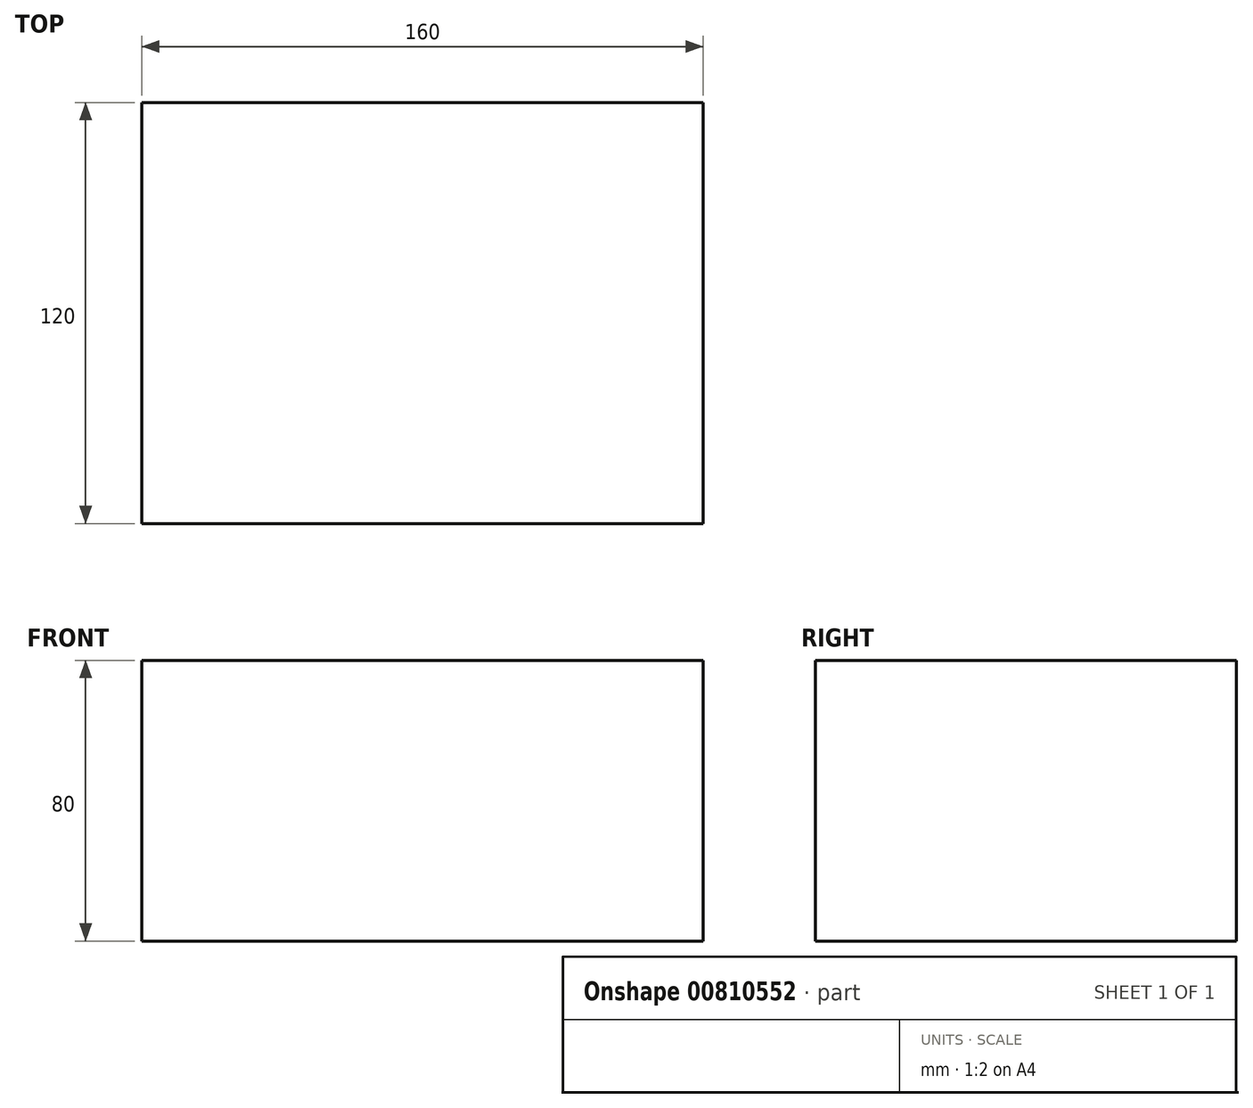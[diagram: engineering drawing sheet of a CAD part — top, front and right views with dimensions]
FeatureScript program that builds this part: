
annotation { "Feature Type Name" : "Feature", "Feature Type Description" : "" }
export const myFeature = defineFeature(function(context is Context, id is Id, definition is map)
    precondition{}
    {
        {
            var Q0;
            Q0=qCreatedBy(makeId("Front.planeOp"),FACE);
            var sketch = newSketch(context, id + "F0", { "sketchPlane" : qUnion([Q0])});
            skLineSegment(sketch, "E0.bottom", {"start": v(80, 40) * mm, "end": v(-80, 40) * mm});
            skLineSegment(sketch, "E0.top", {"start": v(80, -40) * mm, "end": v(-80, -40) * mm});
            skLineSegment(sketch, "E0.left", {"start": v(80, 40) * mm, "end": v(80, -40) * mm});
            skLineSegment(sketch, "E0.right", {"start": v(-80, 40) * mm, "end": v(-80, -40) * mm});
            skPoint(sketch, "E0.middle", {"position": v(0, 0) * mm});
            skSolve(sketch);
        }
        {
            var Q0;
            Q0 = qSketchRegion(id + "F0", true);
            extrude(context, id + "F1", {"entities" : qUnion([Q0]), "endBound" : BoundingType.SYMMETRIC, "depth" : 120 * mm, "offsetDistance" : 25 * mm});
        }
    });
